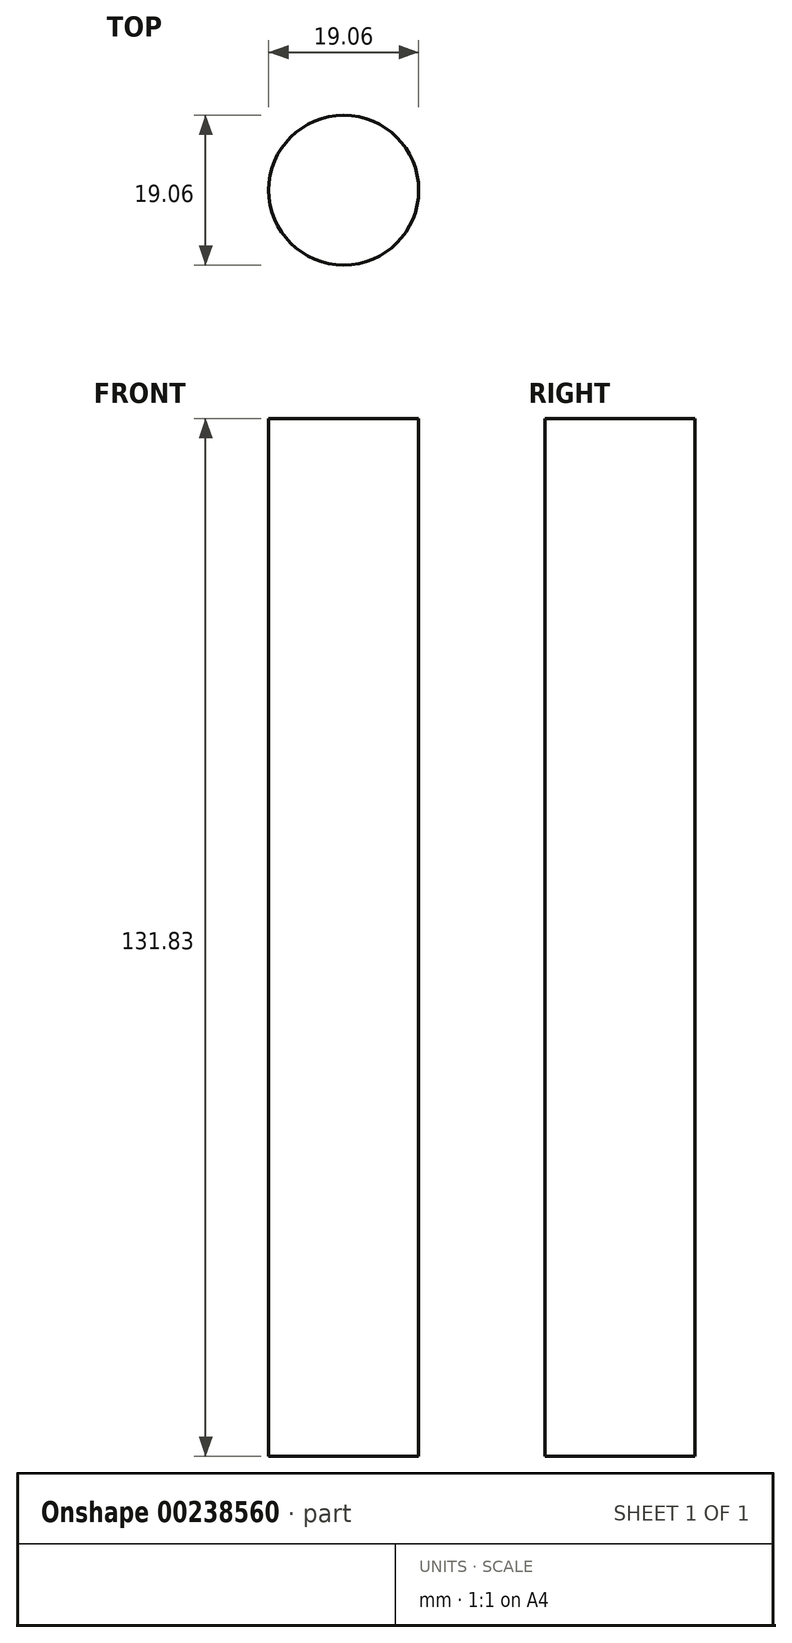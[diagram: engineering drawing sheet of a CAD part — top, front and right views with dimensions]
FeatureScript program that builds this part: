
annotation { "Feature Type Name" : "Feature", "Feature Type Description" : "" }
export const myFeature = defineFeature(function(context is Context, id is Id, definition is map)
    precondition{}
    {
        {
            var Q0;
            Q0=qCreatedBy(makeId("Top.planeOp"),FACE);
            var sketch = newSketch(context, id + "F0", { "sketchPlane" : qUnion([Q0])});
            skCircle(sketch, "E0", {"center": v(0, 0) * mm, "radius": 9.53 * mm});
            skSolve(sketch);
        }
        {
            var Q0;
            Q0 = qSketchRegion(id + "F0", true);
            extrude(context, id + "F1", {"entities" : qUnion([Q0]), "depth" : 131.83 * mm});
        }
    });
